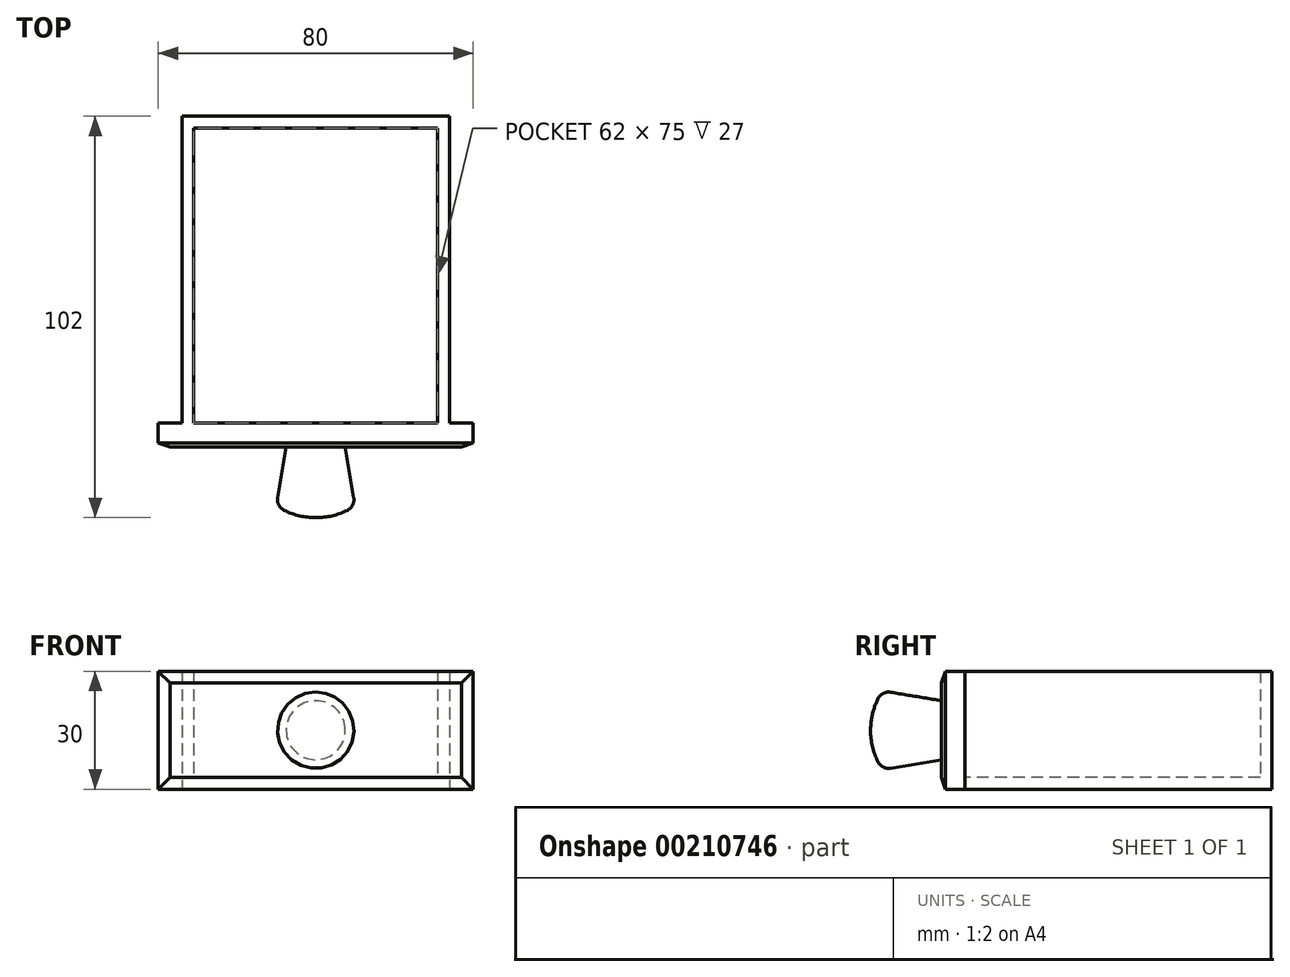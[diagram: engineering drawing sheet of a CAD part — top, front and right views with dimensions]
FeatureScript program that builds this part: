
annotation { "Feature Type Name" : "Feature", "Feature Type Description" : "" }
export const myFeature = defineFeature(function(context is Context, id is Id, definition is map)
    precondition{}
    {
        {
            var Q0;
            Q0=qCreatedBy(makeId("Top.planeOp"),FACE);
            var sketch = newSketch(context, id + "F0", { "sketchPlane" : qUnion([Q0])});
            skLineSegment(sketch, "E0.bottom", {"start": v(-34, 78) * mm, "end": v(34, 78) * mm});
            skLineSegment(sketch, "E0.top", {"start": v(-34, 0) * mm, "end": v(34, 0) * mm});
            skLineSegment(sketch, "E0.left", {"start": v(-34, 78) * mm, "end": v(-34, 0) * mm});
            skLineSegment(sketch, "E0.right", {"start": v(34, 78) * mm, "end": v(34, 0) * mm});
            skSolve(sketch);
        }
        {
            var Q0;
            Q0 = qSketchRegion(id + "F0", true);
            extrude(context, id + "F1", {"entities" : qUnion([Q0]), "depth" : 30 * mm});
        }
        {
            var Q0;
            Q0=makeQuery(id+"F1.opExtrude","CAP_FACE",FACE,{"disambiguationData":[OSD([sQuery(id+"F0.wireOp",EDGE,"E0.bottom"),sQuery(id+"F0.wireOp",EDGE,"E0.top"),sQuery(id+"F0.wireOp",EDGE,"E0.left"),sQuery(id+"F0.wireOp",EDGE,"E0.right")])],"isStart":false});
            var Q1;
            Q1=makeQuery(id+"F1.opExtrude","SWEPT_FACE",FACE,{"disambiguationData":[OSD([sQuery(id+"F0.wireOp",EDGE,"E0.top")])]});
            shell(context, id + "F2", {"entities" : qUnion([Q0, Q1]), "thickness" : 3 * mm});
        }
        {
            var Q0;
            Q0=qCreatedBy(makeId("Front.planeOp"),FACE);
            var sketch = newSketch(context, id + "F3", { "sketchPlane" : qUnion([Q0])});
            skLineSegment(sketch, "E1.bottom", {"start": v(-40, 30) * mm, "end": v(40, 30) * mm});
            skLineSegment(sketch, "E1.top", {"start": v(-40, 0) * mm, "end": v(40, 0) * mm});
            skLineSegment(sketch, "E1.left", {"start": v(-40, 30) * mm, "end": v(-40, 0) * mm});
            skLineSegment(sketch, "E1.right", {"start": v(40, 30) * mm, "end": v(40, 0) * mm});
            skSolve(sketch);
        }
        {
            var Q0;
            Q0 = qSketchRegion(id + "F3", true);
            extrude(context, id + "F4", {"entities" : qUnion([Q0]), "operationType" : NewBodyOperationType.ADD, "depth" : 6 * mm});
        }
        {
            var Q0;
            Q0=makeQuery(id+"F4.opExtrude","CAP_FACE",FACE,{"disambiguationData":[OSD([sQuery(id+"F3.wireOp",EDGE,"E1.bottom"),sQuery(id+"F3.wireOp",EDGE,"E1.top"),sQuery(id+"F3.wireOp",EDGE,"E1.left"),sQuery(id+"F3.wireOp",EDGE,"E1.right")])],"isStart":false});
            chamfer(context, id + "F5", {"entities" : qUnion([Q0]), "chamferType" : ChamferType.TWO_OFFSETS, "width1" : 1 * mm, "oppositeDirection" : false, "width2" : 3 * mm, "tangentPropagation" : true});
        }
        {
            var Q0;
            Q0=qCreatedBy(makeId("Right.planeOp"),FACE);
            var sketch = newSketch(context, id + "F6", { "sketchPlane" : qUnion([Q0])});
            skLineSegment(sketch, "E2", {"start": v(-6, 15) * mm, "end": v(-37.94, 15) * mm, "construction": true});
            skArc(sketch, "E3", {"start": v(-24, 15) * mm, "mid": v(-23.22, 20.22) * mm, "end": v(-20.97, 25) * mm});
            skLineSegment(sketch, "E4", {"start": v(-24, 15) * mm, "end": v(-6, 15) * mm});
            skLineSegment(sketch, "E5", {"start": v(-6, 22.5) * mm, "end": v(-20.97, 25) * mm});
            skLineSegment(sketch, "E6", {"start": v(-6, 15) * mm, "end": v(-6, 22.5) * mm});
            skSolve(sketch);
        }
        {
            var Q0;
            Q0 = qSketchRegion(id + "F6", true);
            var Q1;
            Q1=sQuery(id+"F6.wireOp",EDGE,"E2");
            revolve(context, id + "F7", {"operationType" : NewBodyOperationType.ADD, "entities" : qUnion([Q0]), "axis" : qUnion([Q1]), "revolveType" : RevolveType.FULL});
        }
        {
            var Q0;
            Q0=makeQuery(id+"F7.opRevolve","SWEPT_EDGE",EDGE,{"disambiguationData":[OSD([sQuery(id+"F6.wireOp",EDGE,"E3"),sQuery(id+"F6.wireOp",EDGE,"E5")])]});
            fillet(context, id + "F8", {"entities" : qUnion([Q0]), "radius" : 3 * mm, "tangentPropagation" : true, "allowEdgeOverflow" : false});
        }
    });
